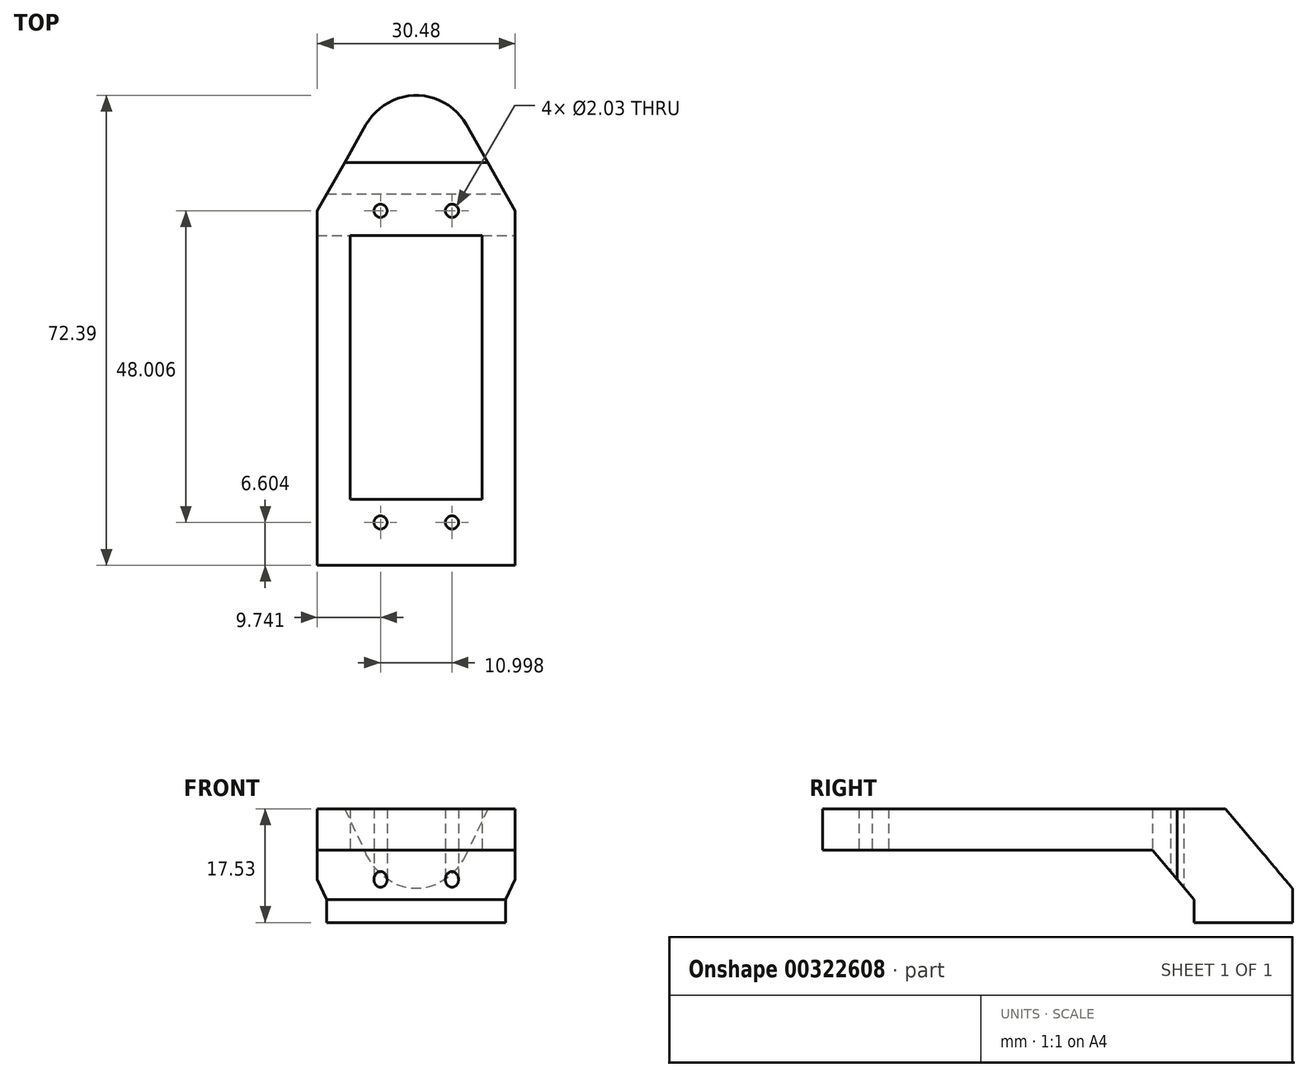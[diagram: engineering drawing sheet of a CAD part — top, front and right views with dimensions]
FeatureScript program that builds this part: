
annotation { "Feature Type Name" : "Feature", "Feature Type Description" : "" }
export const myFeature = defineFeature(function(context is Context, id is Id, definition is map)
    precondition{}
    {
        {
            var Q0;
            Q0=qCreatedBy(makeId("Top.planeOp"),FACE);
            var sketch = newSketch(context, id + "F0", { "sketchPlane" : qUnion([Q0])});
            skLineSegment(sketch, "E0", {"start": v(-15.24, 13.97) * mm, "end": v(-15.24, -40.64) * mm});
            skLineSegment(sketch, "E1", {"start": v(-15.24, -40.64) * mm, "end": v(15.24, -40.64) * mm});
            skLineSegment(sketch, "E2", {"start": v(15.24, -40.64) * mm, "end": v(15.24, 13.97) * mm});
            skCircle(sketch, "E3", {"center": v(0, 22.86) * mm, "radius": 3.81 * mm, "construction": true});
            skLineSegment(sketch, "E4.bottom", {"start": v(-10.16, 10.16) * mm, "end": v(10.16, 10.16) * mm});
            skLineSegment(sketch, "E4.top", {"start": v(-10.16, -30.48) * mm, "end": v(10.16, -30.48) * mm});
            skLineSegment(sketch, "E4.left", {"start": v(-10.16, 10.16) * mm, "end": v(-10.16, -30.48) * mm});
            skLineSegment(sketch, "E4.right", {"start": v(10.16, 10.16) * mm, "end": v(10.16, -30.48) * mm});
            skCircle(sketch, "E5", {"center": v(0, 0) * mm, "radius": 6.35 * mm, "construction": true});
            skLineSegment(sketch, "E6", {"start": v(-15.24, 13.97) * mm, "end": v(15.24, 13.97) * mm, "construction": true});
            skLineSegment(sketch, "E7", {"start": v(-15.24, 0) * mm, "end": v(0, 0) * mm, "construction": true});
            skLineSegment(sketch, "E8", {"start": v(0, 0) * mm, "end": v(15.24, 0) * mm, "construction": true});
            skLineSegment(sketch, "E9", {"start": v(-15.24, -30.48) * mm, "end": v(-10.16, -30.48) * mm, "construction": true});
            skLineSegment(sketch, "E10", {"start": v(10.16, -30.48) * mm, "end": v(15.24, -30.48) * mm, "construction": true});
            skLineSegment(sketch, "E11", {"start": v(-15.24, 13.97) * mm, "end": v(-7.74, 27.24) * mm});
            skLineSegment(sketch, "E12", {"start": v(15.24, 13.97) * mm, "end": v(7.74, 27.24) * mm});
            skArc(sketch, "E13", {"start": v(7.74, 27.24) * mm, "mid": v(0, 31.75) * mm, "end": v(-7.74, 27.24) * mm});
            skCircle(sketch, "E14", {"center": v(-5.5, -34.04) * mm, "radius": 1.02 * mm});
            skCircle(sketch, "E15", {"center": v(5.5, -34.04) * mm, "radius": 1.02 * mm});
            skCircle(sketch, "E16", {"center": v(-5.5, 13.97) * mm, "radius": 1.02 * mm});
            skCircle(sketch, "E17", {"center": v(5.5, 13.97) * mm, "radius": 1.02 * mm});
            skLineSegment(sketch, "E18", {"start": v(-10.16, 10.16) * mm, "end": v(-5.5, 13.97) * mm, "construction": true});
            skLineSegment(sketch, "E19", {"start": v(5.5, 13.97) * mm, "end": v(10.16, 10.16) * mm, "construction": true});
            skLineSegment(sketch, "E20", {"start": v(-5.5, -34.04) * mm, "end": v(-5.5, 13.97) * mm, "construction": true});
            skLineSegment(sketch, "E21", {"start": v(5.5, 13.97) * mm, "end": v(5.5, -34.04) * mm, "construction": true});
            skLineSegment(sketch, "E22", {"start": v(0, 22.86) * mm, "end": v(0, 31.75) * mm});
            skSolve(sketch);
        }
        {
            var Q0;
            Q0 = qSketchRegion(id + "F0", true);
            extrude(context, id + "F1", {"entities" : qUnion([Q0]), "depth" : 17.53 * mm});
        }
        {
            var Q0;
            Q0=makeQuery(id+"F1.opExtrude","SWEPT_FACE",FACE,{"disambiguationData":[OSD([sQuery(id+"F0.wireOp",EDGE,"E2")])]});
            var sketch = newSketch(context, id + "F2", { "sketchPlane" : qUnion([Q0])});
            skLineSegment(sketch, "E23", {"start": v(-40.64, 17.53) * mm, "end": v(-40.64, 11.18) * mm});
            skLineSegment(sketch, "E24", {"start": v(-40.64, 11.18) * mm, "end": v(10.16, 11.18) * mm});
            skLineSegment(sketch, "E25", {"start": v(10.16, 11.18) * mm, "end": v(16.55, 3.56) * mm});
            skLineSegment(sketch, "E26", {"start": v(16.55, 3.56) * mm, "end": v(16.55, 0) * mm});
            skLineSegment(sketch, "E27", {"start": v(16.55, 0) * mm, "end": v(31.75, 0) * mm});
            skLineSegment(sketch, "E28", {"start": v(31.75, 0) * mm, "end": v(31.75, 5.2) * mm});
            skLineSegment(sketch, "E29", {"start": v(31.75, 5.2) * mm, "end": v(21.41, 17.53) * mm});
            skLineSegment(sketch, "E30", {"start": v(21.41, 17.53) * mm, "end": v(-40.64, 17.53) * mm});
            skSolve(sketch);
        }
        {
            var Q0;
            Q0 = qSketchRegion(id + "F2", true);
            extrude(context, id + "F3", {"entities" : qUnion([Q0]), "operationType" : NewBodyOperationType.INTERSECT, "endBound" : BoundingType.THROUGH_ALL, "oppositeDirection" : true, "depth" : 25.4 * mm});
        }
    });
